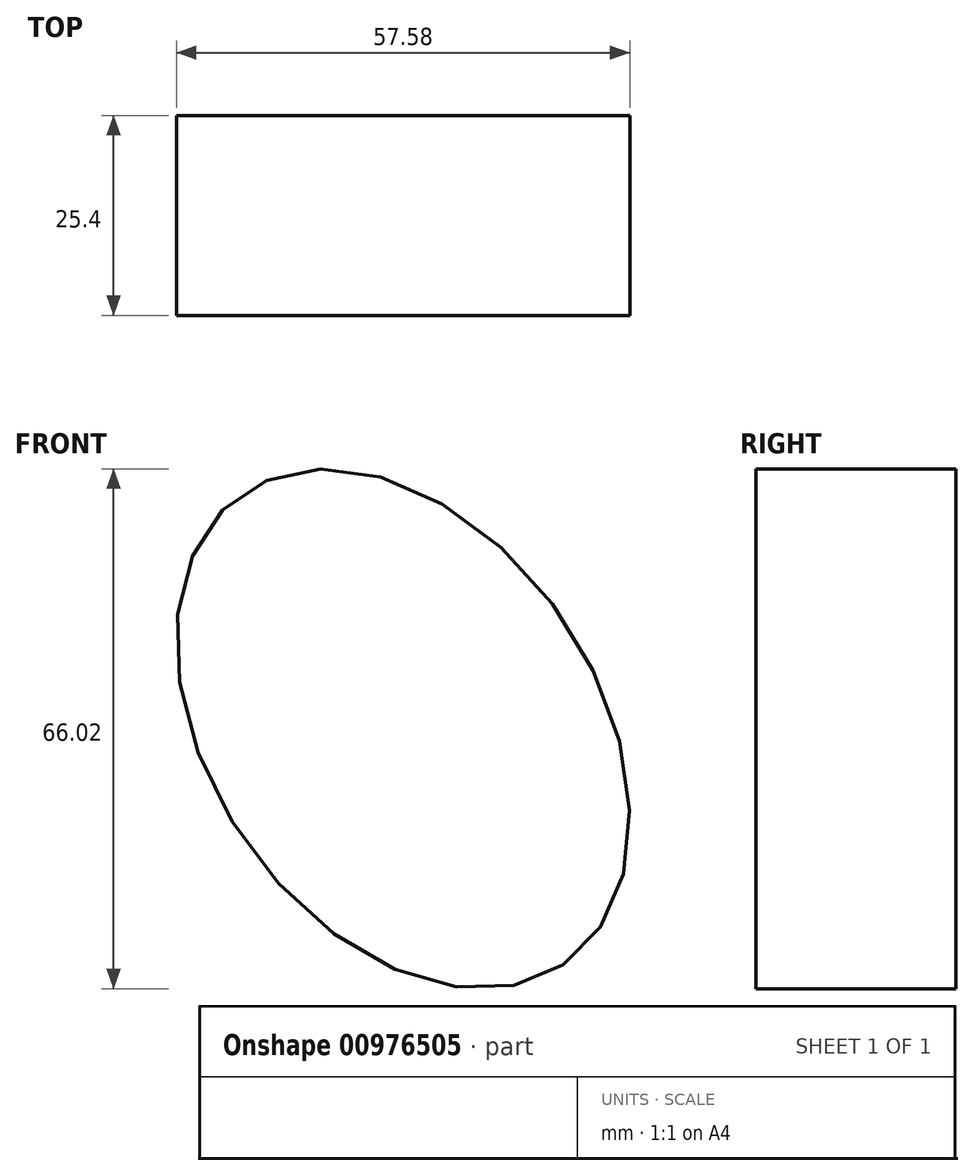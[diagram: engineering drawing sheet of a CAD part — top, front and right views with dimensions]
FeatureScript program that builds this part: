
annotation { "Feature Type Name" : "Feature", "Feature Type Description" : "" }
export const myFeature = defineFeature(function(context is Context, id is Id, definition is map)
    precondition{}
    {
        {
            var Q0;
            Q0=qCreatedBy(makeId("Front.planeOp"),FACE);
            var sketch = newSketch(context, id + "F0", { "sketchPlane" : qUnion([Q0])});
            skEllipse(sketch, "E0", {"center": v(-27.05, 23.75) * mm, "majorRadius": 36.21 * mm, "minorRadius": 24.65 * mm, "majorAxis": v(0.56, -0.83)});
            skSolve(sketch);
        }
        {
            var Q0;
            Q0 = qSketchRegion(id + "F0", true);
            extrude(context, id + "F1", {"entities" : qUnion([Q0]), "depth" : 25.4 * mm, "offsetDistance" : 25.4 * mm});
        }
    });
